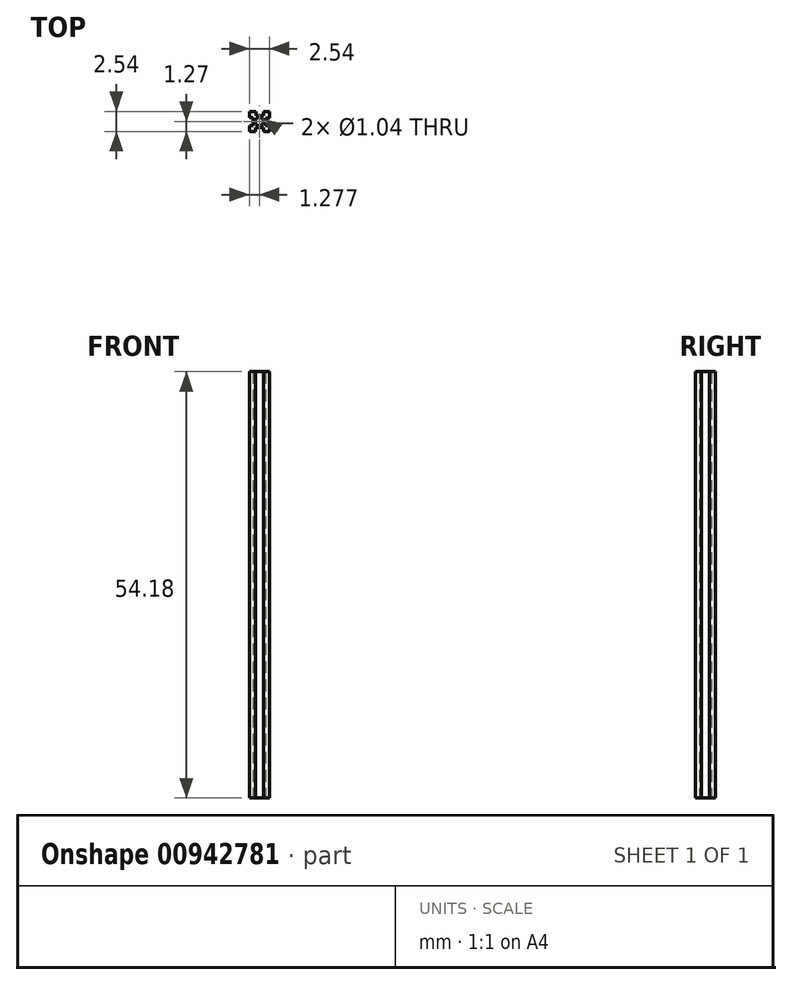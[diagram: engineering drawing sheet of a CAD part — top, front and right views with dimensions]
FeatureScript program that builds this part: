
annotation { "Feature Type Name" : "Feature", "Feature Type Description" : "" }
export const myFeature = defineFeature(function(context is Context, id is Id, definition is map)
    precondition{}
    {
        {
            var Q0;
            Q0=qCreatedBy(makeId("Top.planeOp"),FACE);
            var sketch = newSketch(context, id + "F0", { "sketchPlane" : qUnion([Q0])});
            skLineSegment(sketch, "E0.bottom", {"start": v(0, 0) * mm, "end": v(2.54, 0) * mm});
            skLineSegment(sketch, "E0.top", {"start": v(0, 2.54) * mm, "end": v(2.54, 2.54) * mm});
            skLineSegment(sketch, "E0.left", {"start": v(0, 0) * mm, "end": v(0, 2.54) * mm});
            skLineSegment(sketch, "E0.right", {"start": v(2.54, 0) * mm, "end": v(2.54, 2.54) * mm});
            skCircle(sketch, "E1", {"center": v(1.28, 1.27) * mm, "radius": 0.52 * mm});
            skPoint(sketch, "E1.centerSnap0", {"position": v(0, 1.27) * mm});
            skLineSegment(sketch, "E2.bottom", {"start": v(0.83, 2.54) * mm, "end": v(1.82, 2.54) * mm});
            skLineSegment(sketch, "E2.top", {"start": v(0.83, 2.03) * mm, "end": v(1.82, 2.03) * mm});
            skLineSegment(sketch, "E2.left", {"start": v(0.83, 2.54) * mm, "end": v(0.83, 2.03) * mm});
            skLineSegment(sketch, "E2.right", {"start": v(1.82, 2.54) * mm, "end": v(1.82, 2.03) * mm});
            skLineSegment(sketch, "E3.bottom", {"start": v(2.54, 1.72) * mm, "end": v(2.03, 1.72) * mm});
            skLineSegment(sketch, "E3.top", {"start": v(2.54, 0.75) * mm, "end": v(2.03, 0.75) * mm});
            skLineSegment(sketch, "E3.left", {"start": v(2.54, 1.72) * mm, "end": v(2.54, 0.75) * mm});
            skLineSegment(sketch, "E3.right", {"start": v(2.03, 1.72) * mm, "end": v(2.03, 0.75) * mm});
            skLineSegment(sketch, "E4.bottom", {"start": v(1.82, 0) * mm, "end": v(0.8, 0) * mm});
            skLineSegment(sketch, "E4.top", {"start": v(1.82, 0.52) * mm, "end": v(0.8, 0.52) * mm});
            skLineSegment(sketch, "E4.left", {"start": v(1.82, 0) * mm, "end": v(1.82, 0.52) * mm});
            skLineSegment(sketch, "E4.right", {"start": v(0.8, 0) * mm, "end": v(0.8, 0.52) * mm});
            skLineSegment(sketch, "E5.bottom", {"start": v(0, 0.75) * mm, "end": v(0.5, 0.75) * mm});
            skLineSegment(sketch, "E5.top", {"start": v(0, 1.77) * mm, "end": v(0.5, 1.77) * mm});
            skLineSegment(sketch, "E5.left", {"start": v(0, 0.75) * mm, "end": v(0, 1.77) * mm});
            skLineSegment(sketch, "E5.right", {"start": v(0.5, 0.75) * mm, "end": v(0.5, 1.77) * mm});
            skSolve(sketch);
        }
        {
            var Q0;
            Q0=makeQuery(id+"F0.imprint","IMPRINT",FACE,{"disambiguationData":[TD([[makeQuery(id+"F0.imprint","IMPRINT",EDGE,{"derivedFrom":sQuery(id+"F0.wireOp",EDGE,"E1")}),-1.0]])]});
            extrude(context, id + "F1", {"entities" : qUnion([Q0]), "depth" : 54.18 * mm, "offsetDistance" : 25.4 * mm});
        }
    });
